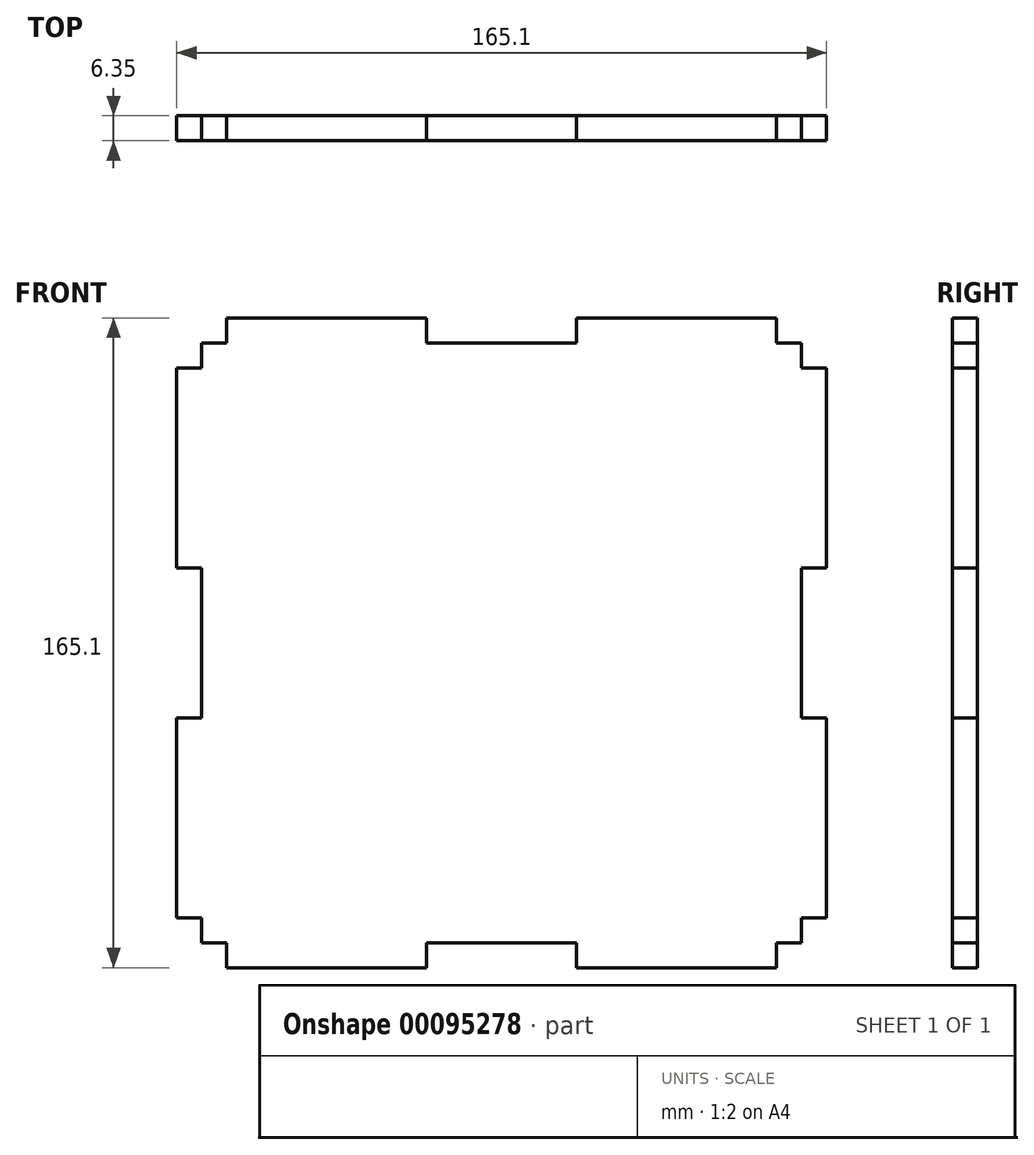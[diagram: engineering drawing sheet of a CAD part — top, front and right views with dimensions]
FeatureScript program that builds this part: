
annotation { "Feature Type Name" : "Feature", "Feature Type Description" : "" }
export const myFeature = defineFeature(function(context is Context, id is Id, definition is map)
    precondition{}
    {
        {
            var Q0;
            Q0=qCreatedBy(makeId("Front.planeOp"),FACE);
            var sketch = newSketch(context, id + "F0", { "sketchPlane" : qUnion([Q0])});
            skLineSegment(sketch, "E0.bottom", {"start": v(-76.2, 76.2) * mm, "end": v(76.2, 76.2) * mm});
            skLineSegment(sketch, "E0.top", {"start": v(-76.2, -76.2) * mm, "end": v(76.2, -76.2) * mm});
            skLineSegment(sketch, "E0.left", {"start": v(-76.2, 76.2) * mm, "end": v(-76.2, -76.2) * mm});
            skLineSegment(sketch, "E0.right", {"start": v(76.2, 76.2) * mm, "end": v(76.2, -76.2) * mm});
            skPoint(sketch, "E0.middle", {"position": v(0, 0) * mm});
            skLineSegment(sketch, "E1.bottom", {"start": v(-69.85, 76.2) * mm, "end": v(-19.05, 76.2) * mm});
            skLineSegment(sketch, "E1.top", {"start": v(-69.85, 82.55) * mm, "end": v(-19.05, 82.55) * mm});
            skLineSegment(sketch, "E1.left", {"start": v(-69.85, 76.2) * mm, "end": v(-69.85, 82.55) * mm});
            skLineSegment(sketch, "E1.right", {"start": v(-19.05, 76.2) * mm, "end": v(-19.05, 82.55) * mm});
            skLineSegment(sketch, "E2", {"start": v(-76.2, 76.2) * mm, "end": v(76.2, -76.2) * mm, "construction": true});
            skLineSegment(sketch, "E3.MirrorCS", {"start": v(-76.2, 69.85) * mm, "end": v(-76.2, 19.05) * mm});
            skLineSegment(sketch, "E4.MirrorCS", {"start": v(-82.55, 69.85) * mm, "end": v(-82.55, 19.05) * mm});
            skLineSegment(sketch, "E5.MirrorCS", {"start": v(-76.2, 69.85) * mm, "end": v(-82.55, 69.85) * mm});
            skLineSegment(sketch, "E6.MirrorCS", {"start": v(-76.2, 19.05) * mm, "end": v(-82.55, 19.05) * mm});
            skLineSegment(sketch, "E7.MirrorCS", {"start": v(69.85, 82.55) * mm, "end": v(19.05, 82.55) * mm});
            skLineSegment(sketch, "E8.MirrorCS", {"start": v(69.85, 76.2) * mm, "end": v(69.85, 82.55) * mm});
            skLineSegment(sketch, "E9.MirrorCS", {"start": v(19.05, 76.2) * mm, "end": v(19.05, 82.55) * mm});
            skLineSegment(sketch, "E10.MirrorCS", {"start": v(-76.2, -19.05) * mm, "end": v(-82.55, -19.05) * mm});
            skLineSegment(sketch, "E11.MirrorCS", {"start": v(-82.55, -69.85) * mm, "end": v(-82.55, -19.05) * mm});
            skLineSegment(sketch, "E12.MirrorCS", {"start": v(-76.2, -69.85) * mm, "end": v(-82.55, -69.85) * mm});
            skLineSegment(sketch, "E13.MirrorCS", {"start": v(-69.85, -76.2) * mm, "end": v(-69.85, -82.55) * mm});
            skLineSegment(sketch, "E14.MirrorCS", {"start": v(-69.85, -82.55) * mm, "end": v(-19.05, -82.55) * mm});
            skLineSegment(sketch, "E15.MirrorCS", {"start": v(-19.05, -76.2) * mm, "end": v(-19.05, -82.55) * mm});
            skLineSegment(sketch, "E16.MirrorCS", {"start": v(19.05, -76.2) * mm, "end": v(19.05, -82.55) * mm});
            skLineSegment(sketch, "E17.MirrorCS", {"start": v(69.85, -82.55) * mm, "end": v(19.05, -82.55) * mm});
            skLineSegment(sketch, "E18.MirrorCS", {"start": v(69.85, -76.2) * mm, "end": v(69.85, -82.55) * mm});
            skLineSegment(sketch, "E19.MirrorCS", {"start": v(82.55, 69.85) * mm, "end": v(82.55, 19.05) * mm});
            skLineSegment(sketch, "E20.MirrorCS", {"start": v(76.2, 19.05) * mm, "end": v(82.55, 19.05) * mm});
            skLineSegment(sketch, "E21.MirrorCS", {"start": v(76.2, 69.85) * mm, "end": v(82.55, 69.85) * mm});
            skLineSegment(sketch, "E22.MirrorCS", {"start": v(76.2, -19.05) * mm, "end": v(82.55, -19.05) * mm});
            skLineSegment(sketch, "E23.MirrorCS", {"start": v(82.55, -69.85) * mm, "end": v(82.55, -19.05) * mm});
            skLineSegment(sketch, "E24.MirrorCS", {"start": v(76.2, -69.85) * mm, "end": v(82.55, -69.85) * mm});
            skSolve(sketch);
        }
        {
            var Q0;
            Q0 = qSketchRegion(id + "F0", true);
            extrude(context, id + "F1", {"entities" : qUnion([Q0]), "depth" : 6.35 * mm});
        }
    });
